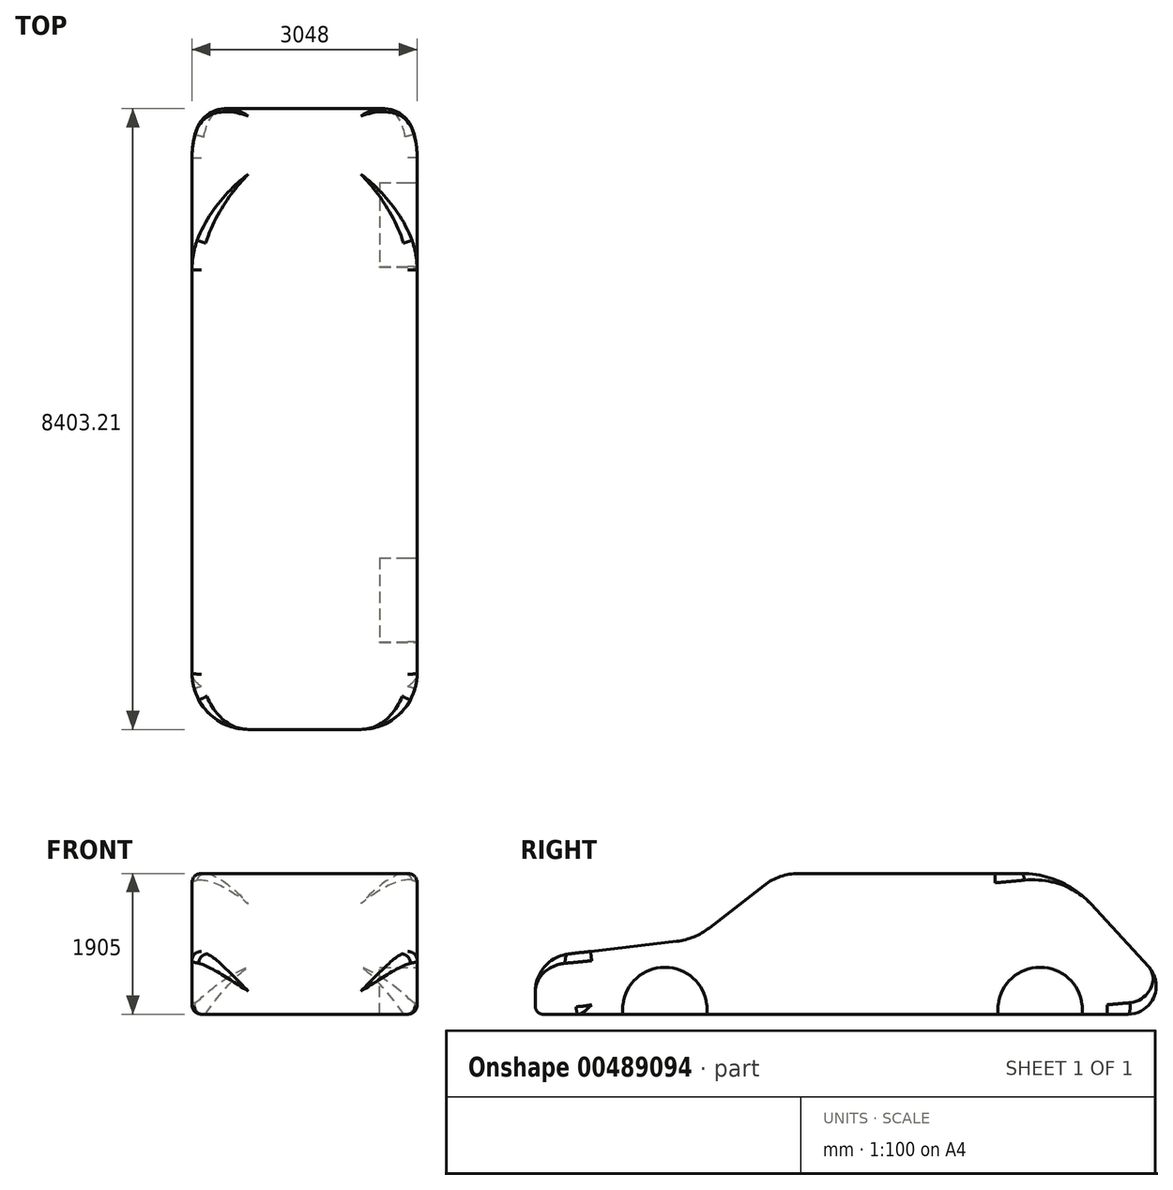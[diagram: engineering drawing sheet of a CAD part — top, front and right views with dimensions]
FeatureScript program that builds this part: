
annotation { "Feature Type Name" : "Feature", "Feature Type Description" : "" }
export const myFeature = defineFeature(function(context is Context, id is Id, definition is map)
    precondition{}
    {
        {
            var Q0;
            Q0=qCreatedBy(makeId("Front.planeOp"),FACE);
            var sketch = newSketch(context, id + "F0", { "sketchPlane" : qUnion([Q0])});
            skLineSegment(sketch, "E0.bottom", {"start": v(36.45, 57.67) * mm, "end": v(315.85, 57.67) * mm});
            skLineSegment(sketch, "E0.top", {"start": v(36.45, -94.73) * mm, "end": v(315.85, -94.73) * mm});
            skLineSegment(sketch, "E0.left", {"start": v(-14.35, 6.87) * mm, "end": v(-14.35, -43.93) * mm});
            skLineSegment(sketch, "E0.right", {"start": v(366.65, 6.87) * mm, "end": v(366.65, -43.93) * mm});
            skPoint(sketch, "E1.visualSharp", {"position": v(-14.35, 57.67) * mm});
            skArc(sketch, "E1.filletArc", {"start": v(36.45, 57.67) * mm, "mid": v(0.53, 42.8) * mm, "end": v(-14.35, 6.87) * mm});
            skPoint(sketch, "E2.visualSharp", {"position": v(-14.35, -94.73) * mm});
            skArc(sketch, "E2.filletArc", {"start": v(-14.35, -43.93) * mm, "mid": v(0.53, -79.85) * mm, "end": v(36.45, -94.73) * mm});
            skPoint(sketch, "E3.visualSharp", {"position": v(366.65, -94.73) * mm});
            skArc(sketch, "E3.filletArc", {"start": v(315.85, -94.73) * mm, "mid": v(351.77, -79.85) * mm, "end": v(366.65, -43.93) * mm});
            skPoint(sketch, "E4.visualSharp", {"position": v(366.65, 57.67) * mm});
            skArc(sketch, "E4.filletArc", {"start": v(366.65, 6.87) * mm, "mid": v(351.77, 42.8) * mm, "end": v(315.85, 57.67) * mm});
            skLineSegment(sketch, "E5", {"start": v(-69.05, -475.73) * mm, "end": v(416.53, -475.73) * mm});
            skSolve(sketch);
        }
        {
            var Q0;
            Q0=qCreatedBy(makeId("Front.planeOp"),FACE);
            var sketch = newSketch(context, id + "F1", { "sketchPlane" : qUnion([Q0])});
            skLineSegment(sketch, "E6", {"start": v(246.45, -145.53) * mm, "end": v(271.85, -145.53) * mm});
            skLineSegment(sketch, "E7", {"start": v(14.45, -107.43) * mm, "end": v(-10.48, -64.25) * mm});
            skLineSegment(sketch, "E8", {"start": v(366.62, -57.58) * mm, "end": v(337.84, -107.43) * mm});
            skArc(sketch, "E9.filletArc", {"start": v(14.45, -107.43) * mm, "mid": v(42.34, -135.32) * mm, "end": v(80.44, -145.53) * mm});
            skArc(sketch, "E10.filletArc", {"start": v(271.85, -145.53) * mm, "mid": v(309.95, -135.32) * mm, "end": v(337.84, -107.43) * mm});
            skLineSegment(sketch, "E11", {"start": v(195.65, -196.33) * mm, "end": v(195.65, -399.53) * mm});
            skArc(sketch, "E12.filletArc", {"start": v(246.45, -145.53) * mm, "mid": v(210.53, -160.4) * mm, "end": v(195.65, -196.33) * mm});
            skLineSegment(sketch, "E13", {"start": v(80.44, -145.53) * mm, "end": v(271.85, -145.53) * mm});
            skSolve(sketch);
        }
        {
            var Q0;
            Q0=qCreatedBy(makeId("Right.planeOp"),FACE);
            var sketch = newSketch(context, id + "F2", { "sketchPlane" : qUnion([Q0])});
            skLineSegment(sketch, "E14", {"start": v(-3145.84, -762) * mm, "end": v(4774.77, -762) * mm});
            skLineSegment(sketch, "E15", {"start": v(5055.26, -123.15) * mm, "end": v(4268.66, 732.5) * mm});
            skLineSegment(sketch, "E16", {"start": v(3333.7, 1143) * mm, "end": v(316, 1143) * mm});
            skLineSegment(sketch, "E17", {"start": v(-151.82, 982.49) * mm, "end": v(-892.74, 406.2) * mm});
            skLineSegment(sketch, "E18", {"start": v(-3247.44, -660.4) * mm, "end": v(-3247.44, -451.74) * mm});
            skLineSegment(sketch, "E19", {"start": v(-2798.8, 52.78) * mm, "end": v(-1334.67, 225.03) * mm});
            skPoint(sketch, "E20.visualSharp", {"position": v(5642.56, -762) * mm});
            skArc(sketch, "E20.filletArc", {"start": v(4774.77, -762) * mm, "mid": v(5123.63, -534.17) * mm, "end": v(5055.26, -123.15) * mm});
            skPoint(sketch, "E21.visualSharp", {"position": v(3891.3, 1143) * mm});
            skArc(sketch, "E21.filletArc", {"start": v(4268.66, 732.5) * mm, "mid": v(3844.25, 1035.86) * mm, "end": v(3333.7, 1143) * mm});
            skPoint(sketch, "E22.visualSharp", {"position": v(54.56, 1143) * mm});
            skArc(sketch, "E22.filletArc", {"start": v(316, 1143) * mm, "mid": v(68.7, 1101.76) * mm, "end": v(-151.82, 982.49) * mm});
            skPoint(sketch, "E23.visualSharp", {"position": v(-1088.44, 254) * mm});
            skArc(sketch, "E23.filletArc", {"start": v(-1334.67, 225.03) * mm, "mid": v(-1101.3, 285.39) * mm, "end": v(-892.74, 406.2) * mm});
            skPoint(sketch, "E24.visualSharp", {"position": v(-3247.44, 0) * mm});
            skArc(sketch, "E24.filletArc", {"start": v(-2798.8, 52.78) * mm, "mid": v(-3119.06, -114.17) * mm, "end": v(-3247.44, -451.74) * mm});
            skPoint(sketch, "E25.visualSharp", {"position": v(-3247.44, -762) * mm});
            skArc(sketch, "E25.filletArc", {"start": v(-3247.44, -660.4) * mm, "mid": v(-3217.68, -732.24) * mm, "end": v(-3145.84, -762) * mm});
            skSolve(sketch);
        }
        {
            var Q0;
            Q0=makeQuery(id+"F2.imprint","IMPRINT",FACE,{"disambiguationData":[TD([[makeQuery(id+"F2.imprint","IMPRINT",EDGE,{"derivedFrom":sQuery(id+"F2.wireOp",EDGE,"E14")}),1.0]])]});
            extrude(context, id + "F3", {"entities" : qUnion([Q0]), "oppositeDirection" : true, "depth" : 3048 * mm});
        }
        {
            var Q0;
            Q0=makeQuery(id+"F3.opExtrude","SWEPT_FACE",FACE,{"disambiguationData":[OSD([sQuery(id+"F2.wireOp",EDGE,"E15")])]});
            var Q1;
            Q1=makeQuery(id+"F3.opExtrude","SWEPT_FACE",FACE,{"disambiguationData":[OSD([sQuery(id+"F2.wireOp",EDGE,"E18")])]});
            fillet(context, id + "F4", {"entities" : qUnion([Q0, Q1]), "radius" : 762 * mm, "allowEdgeOverflow" : false});
        }
        {
            var Q0;
            Q0=makeQuery(id+"F3.opExtrude","SWEPT_FACE",FACE,{"disambiguationData":[OSD([sQuery(id+"F2.wireOp",EDGE,"E17")])]});
            var Q1;
            Q1=makeQuery(id+"F3.opExtrude","SWEPT_FACE",FACE,{"disambiguationData":[OSD([sQuery(id+"F2.wireOp",EDGE,"E21.filletArc")])]});
            fillet(context, id + "F5", {"entities" : qUnion([Q0, Q1]), "radius" : 127 * mm, "tangentPropagation" : true, "allowEdgeOverflow" : false});
        }
        {
            var Q0;
            Q0=makeQuery(id+"F3.opExtrude","SWEPT_FACE",FACE,{"disambiguationData":[OSD([sQuery(id+"F2.wireOp",EDGE,"E14")])]});
            fillet(context, id + "F6", {"entities" : qUnion([Q0]), "radius" : 127 * mm, "tangentPropagation" : true, "allowEdgeOverflow" : false});
        }
        {
            var Q0;
            Q0=makeQuery(id+"F3.opExtrude","CAP_FACE",FACE,{"disambiguationData":[OSD([sQuery(id+"F2.wireOp",EDGE,"E14"),sQuery(id+"F2.wireOp",EDGE,"E15"),sQuery(id+"F2.wireOp",EDGE,"E16"),sQuery(id+"F2.wireOp",EDGE,"E17"),sQuery(id+"F2.wireOp",EDGE,"E18"),sQuery(id+"F2.wireOp",EDGE,"E19"),sQuery(id+"F2.wireOp",EDGE,"E20.filletArc"),sQuery(id+"F2.wireOp",EDGE,"E21.filletArc"),sQuery(id+"F2.wireOp",EDGE,"E22.filletArc"),sQuery(id+"F2.wireOp",EDGE,"E23.filletArc"),sQuery(id+"F2.wireOp",EDGE,"E24.filletArc"),sQuery(id+"F2.wireOp",EDGE,"E25.filletArc")])],"isStart":true});
            var sketch = newSketch(context, id + "F7", { "sketchPlane" : qUnion([Q0])});
            skCircle(sketch, "E26", {"center": v(-1494.84, -698.5) * mm, "radius": 571.5 * mm});
            skCircle(sketch, "E27", {"center": v(3585.16, -698.5) * mm, "radius": 571.5 * mm});
            skSolve(sketch);
        }
        {
            var Q0;
            {var subQ0=sQuery(id+"F7.wireOp",EDGE,"E26");var subQ1=sQuery(id+"F2.wireOp",EDGE,"E14");var subQ2=makeQuery(id+"F6.opFillet","BLEND_EDGE",EDGE,{"blendedFrom":[makeQuery(id+"F3.opExtrude","CAP_EDGE",EDGE,{"disambiguationData":[OSD([subQ1])],"isStart":true}),makeQuery(id+"F3.opExtrude","CAP_FACE",FACE,{"disambiguationData":[OSD([subQ1,sQuery(id+"F2.wireOp",EDGE,"E15"),sQuery(id+"F2.wireOp",EDGE,"E16"),sQuery(id+"F2.wireOp",EDGE,"E17"),sQuery(id+"F2.wireOp",EDGE,"E18"),sQuery(id+"F2.wireOp",EDGE,"E19"),sQuery(id+"F2.wireOp",EDGE,"E20.filletArc"),sQuery(id+"F2.wireOp",EDGE,"E21.filletArc"),sQuery(id+"F2.wireOp",EDGE,"E22.filletArc"),sQuery(id+"F2.wireOp",EDGE,"E23.filletArc"),sQuery(id+"F2.wireOp",EDGE,"E24.filletArc"),sQuery(id+"F2.wireOp",EDGE,"E25.filletArc")])],"isStart":true})],"blendedInto":[makeQuery(id+"F3.opExtrude","CAP_FACE",FACE,{"disambiguationData":[OSD([subQ1,sQuery(id+"F2.wireOp",EDGE,"E15"),sQuery(id+"F2.wireOp",EDGE,"E16"),sQuery(id+"F2.wireOp",EDGE,"E17"),sQuery(id+"F2.wireOp",EDGE,"E18"),sQuery(id+"F2.wireOp",EDGE,"E19"),sQuery(id+"F2.wireOp",EDGE,"E20.filletArc"),sQuery(id+"F2.wireOp",EDGE,"E21.filletArc"),sQuery(id+"F2.wireOp",EDGE,"E22.filletArc"),sQuery(id+"F2.wireOp",EDGE,"E23.filletArc"),sQuery(id+"F2.wireOp",EDGE,"E24.filletArc"),sQuery(id+"F2.wireOp",EDGE,"E25.filletArc")])],"isStart":true})]});var subQ3=makeQuery(id+"F7.imprint","INTERSECT",VERTEX,{"disambiguationData":[OD(0.0)],"derivedFrom":[subQ2,subQ0]});Q0=makeQuery(id+"F7.imprint","IMPRINT",FACE,{"disambiguationData":[TD([[makeQuery(id+"F7.imprint","IMPRINT",EDGE,{"disambiguationData":[TD([[subQ3,-1.0]])],"derivedFrom":subQ0}),1.0]])]});}
            var Q1;
            {var subQ0=sQuery(id+"F7.wireOp",EDGE,"E26");var subQ1=sQuery(id+"F2.wireOp",EDGE,"E14");var subQ2=makeQuery(id+"F6.opFillet","BLEND_EDGE",EDGE,{"blendedFrom":[makeQuery(id+"F3.opExtrude","CAP_EDGE",EDGE,{"disambiguationData":[OSD([subQ1])],"isStart":true}),makeQuery(id+"F3.opExtrude","CAP_FACE",FACE,{"disambiguationData":[OSD([subQ1,sQuery(id+"F2.wireOp",EDGE,"E15"),sQuery(id+"F2.wireOp",EDGE,"E16"),sQuery(id+"F2.wireOp",EDGE,"E17"),sQuery(id+"F2.wireOp",EDGE,"E18"),sQuery(id+"F2.wireOp",EDGE,"E19"),sQuery(id+"F2.wireOp",EDGE,"E20.filletArc"),sQuery(id+"F2.wireOp",EDGE,"E21.filletArc"),sQuery(id+"F2.wireOp",EDGE,"E22.filletArc"),sQuery(id+"F2.wireOp",EDGE,"E23.filletArc"),sQuery(id+"F2.wireOp",EDGE,"E24.filletArc"),sQuery(id+"F2.wireOp",EDGE,"E25.filletArc")])],"isStart":true})],"blendedInto":[makeQuery(id+"F3.opExtrude","CAP_FACE",FACE,{"disambiguationData":[OSD([subQ1,sQuery(id+"F2.wireOp",EDGE,"E15"),sQuery(id+"F2.wireOp",EDGE,"E16"),sQuery(id+"F2.wireOp",EDGE,"E17"),sQuery(id+"F2.wireOp",EDGE,"E18"),sQuery(id+"F2.wireOp",EDGE,"E19"),sQuery(id+"F2.wireOp",EDGE,"E20.filletArc"),sQuery(id+"F2.wireOp",EDGE,"E21.filletArc"),sQuery(id+"F2.wireOp",EDGE,"E22.filletArc"),sQuery(id+"F2.wireOp",EDGE,"E23.filletArc"),sQuery(id+"F2.wireOp",EDGE,"E24.filletArc"),sQuery(id+"F2.wireOp",EDGE,"E25.filletArc")])],"isStart":true})]});var subQ3=makeQuery(id+"F7.imprint","INTERSECT",VERTEX,{"disambiguationData":[OD(0.0)],"derivedFrom":[subQ2,subQ0]});Q1=makeQuery(id+"F7.imprint","IMPRINT",FACE,{"disambiguationData":[TD([[makeQuery(id+"F7.imprint","IMPRINT",EDGE,{"disambiguationData":[TD([[subQ3,1.0]])],"derivedFrom":subQ0}),1.0]])]});}
            var Q2;
            {var subQ0=sQuery(id+"F7.wireOp",EDGE,"E27");var subQ1=sQuery(id+"F2.wireOp",EDGE,"E14");var subQ2=makeQuery(id+"F6.opFillet","BLEND_EDGE",EDGE,{"blendedFrom":[makeQuery(id+"F3.opExtrude","CAP_EDGE",EDGE,{"disambiguationData":[OSD([subQ1])],"isStart":true}),makeQuery(id+"F3.opExtrude","CAP_FACE",FACE,{"disambiguationData":[OSD([subQ1,sQuery(id+"F2.wireOp",EDGE,"E15"),sQuery(id+"F2.wireOp",EDGE,"E16"),sQuery(id+"F2.wireOp",EDGE,"E17"),sQuery(id+"F2.wireOp",EDGE,"E18"),sQuery(id+"F2.wireOp",EDGE,"E19"),sQuery(id+"F2.wireOp",EDGE,"E20.filletArc"),sQuery(id+"F2.wireOp",EDGE,"E21.filletArc"),sQuery(id+"F2.wireOp",EDGE,"E22.filletArc"),sQuery(id+"F2.wireOp",EDGE,"E23.filletArc"),sQuery(id+"F2.wireOp",EDGE,"E24.filletArc"),sQuery(id+"F2.wireOp",EDGE,"E25.filletArc")])],"isStart":true})],"blendedInto":[makeQuery(id+"F3.opExtrude","CAP_FACE",FACE,{"disambiguationData":[OSD([subQ1,sQuery(id+"F2.wireOp",EDGE,"E15"),sQuery(id+"F2.wireOp",EDGE,"E16"),sQuery(id+"F2.wireOp",EDGE,"E17"),sQuery(id+"F2.wireOp",EDGE,"E18"),sQuery(id+"F2.wireOp",EDGE,"E19"),sQuery(id+"F2.wireOp",EDGE,"E20.filletArc"),sQuery(id+"F2.wireOp",EDGE,"E21.filletArc"),sQuery(id+"F2.wireOp",EDGE,"E22.filletArc"),sQuery(id+"F2.wireOp",EDGE,"E23.filletArc"),sQuery(id+"F2.wireOp",EDGE,"E24.filletArc"),sQuery(id+"F2.wireOp",EDGE,"E25.filletArc")])],"isStart":true})]});var subQ3=makeQuery(id+"F7.imprint","INTERSECT",VERTEX,{"disambiguationData":[OD(0.0)],"derivedFrom":[subQ2,subQ0]});Q2=makeQuery(id+"F7.imprint","IMPRINT",FACE,{"disambiguationData":[TD([[makeQuery(id+"F7.imprint","IMPRINT",EDGE,{"disambiguationData":[TD([[subQ3,1.0]])],"derivedFrom":subQ0}),1.0]])]});}
            var Q3;
            {var subQ0=sQuery(id+"F7.wireOp",EDGE,"E27");var subQ1=sQuery(id+"F2.wireOp",EDGE,"E14");var subQ2=makeQuery(id+"F6.opFillet","BLEND_EDGE",EDGE,{"blendedFrom":[makeQuery(id+"F3.opExtrude","CAP_EDGE",EDGE,{"disambiguationData":[OSD([subQ1])],"isStart":true}),makeQuery(id+"F3.opExtrude","CAP_FACE",FACE,{"disambiguationData":[OSD([subQ1,sQuery(id+"F2.wireOp",EDGE,"E15"),sQuery(id+"F2.wireOp",EDGE,"E16"),sQuery(id+"F2.wireOp",EDGE,"E17"),sQuery(id+"F2.wireOp",EDGE,"E18"),sQuery(id+"F2.wireOp",EDGE,"E19"),sQuery(id+"F2.wireOp",EDGE,"E20.filletArc"),sQuery(id+"F2.wireOp",EDGE,"E21.filletArc"),sQuery(id+"F2.wireOp",EDGE,"E22.filletArc"),sQuery(id+"F2.wireOp",EDGE,"E23.filletArc"),sQuery(id+"F2.wireOp",EDGE,"E24.filletArc"),sQuery(id+"F2.wireOp",EDGE,"E25.filletArc")])],"isStart":true})],"blendedInto":[makeQuery(id+"F3.opExtrude","CAP_FACE",FACE,{"disambiguationData":[OSD([subQ1,sQuery(id+"F2.wireOp",EDGE,"E15"),sQuery(id+"F2.wireOp",EDGE,"E16"),sQuery(id+"F2.wireOp",EDGE,"E17"),sQuery(id+"F2.wireOp",EDGE,"E18"),sQuery(id+"F2.wireOp",EDGE,"E19"),sQuery(id+"F2.wireOp",EDGE,"E20.filletArc"),sQuery(id+"F2.wireOp",EDGE,"E21.filletArc"),sQuery(id+"F2.wireOp",EDGE,"E22.filletArc"),sQuery(id+"F2.wireOp",EDGE,"E23.filletArc"),sQuery(id+"F2.wireOp",EDGE,"E24.filletArc"),sQuery(id+"F2.wireOp",EDGE,"E25.filletArc")])],"isStart":true})]});var subQ3=makeQuery(id+"F7.imprint","INTERSECT",VERTEX,{"disambiguationData":[OD(0.0)],"derivedFrom":[subQ2,subQ0]});Q3=makeQuery(id+"F7.imprint","IMPRINT",FACE,{"disambiguationData":[TD([[makeQuery(id+"F7.imprint","IMPRINT",EDGE,{"disambiguationData":[TD([[subQ3,-1.0]])],"derivedFrom":subQ0}),1.0]])]});}
            extrude(context, id + "F8", {"entities" : qUnion([Q0, Q1, Q2, Q3]), "operationType" : NewBodyOperationType.REMOVE, "oppositeDirection" : true, "depth" : 508 * mm});
        }
    });
